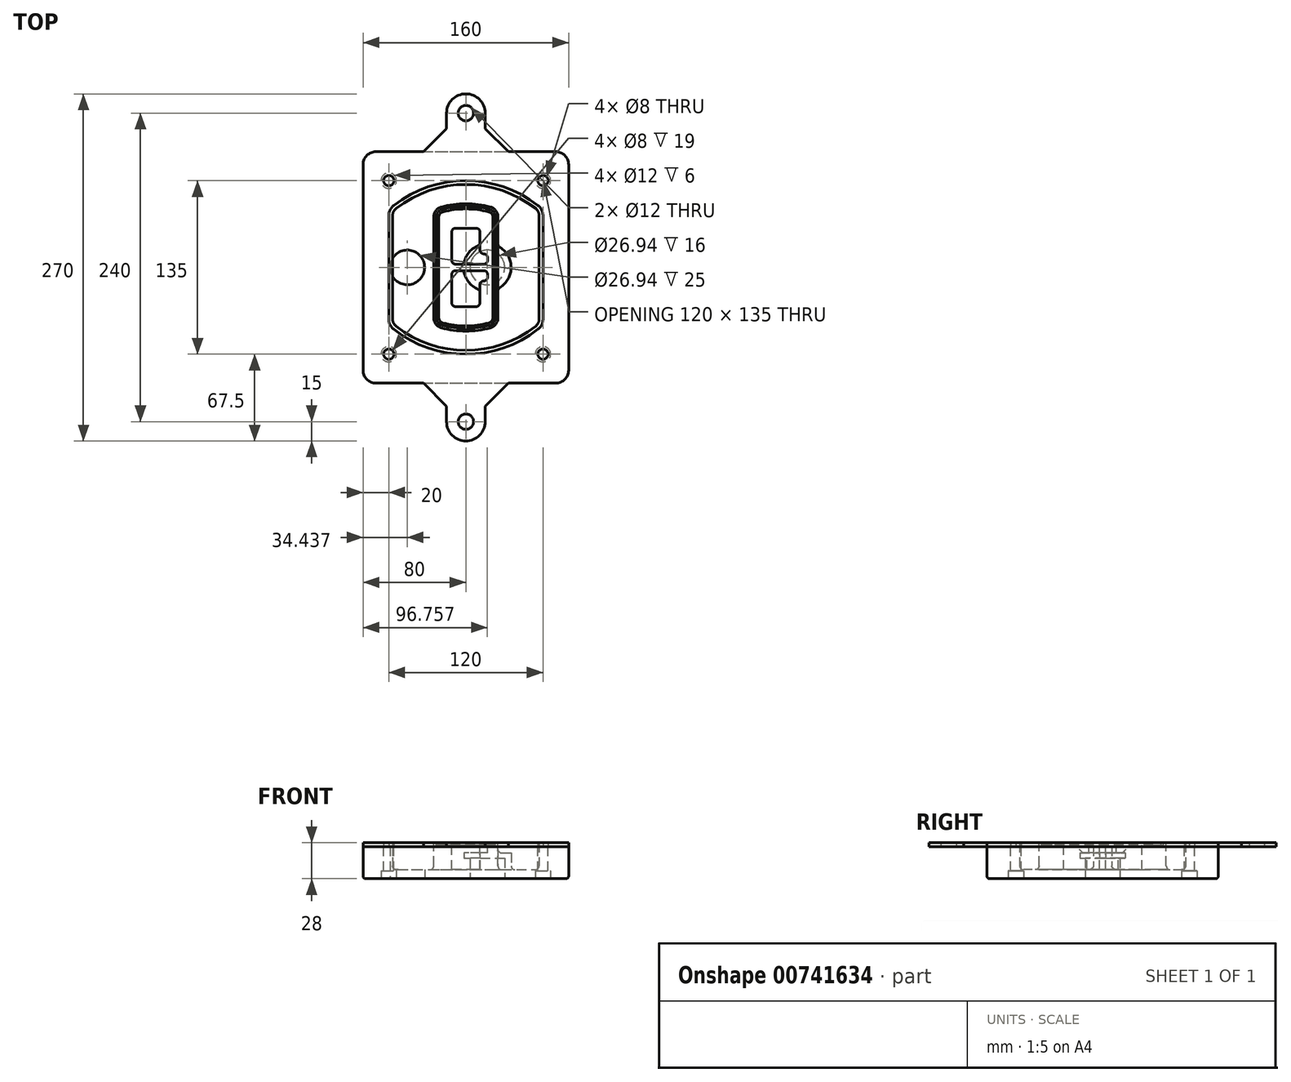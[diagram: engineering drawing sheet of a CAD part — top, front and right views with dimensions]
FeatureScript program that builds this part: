
annotation { "Feature Type Name" : "Feature", "Feature Type Description" : "" }
export const myFeature = defineFeature(function(context is Context, id is Id, definition is map)
    precondition{}
    {
        {
            var Q0;
            Q0=qCreatedBy(makeId("Top.planeOp"),FACE);
            var sketch = newSketch(context, id + "F0", { "sketchPlane" : qUnion([Q0])});
            skPoint(sketch, "E0.rect.middle", {"position": v(0, 0) * mm});
            skLineSegment(sketch, "E1.bottom", {"start": v(-70, -90) * mm, "end": v(70, -90) * mm});
            skLineSegment(sketch, "E1.top", {"start": v(-70, 90) * mm, "end": v(70, 90) * mm});
            skLineSegment(sketch, "E1.left", {"start": v(-80, -80) * mm, "end": v(-80, 80) * mm});
            skLineSegment(sketch, "E1.right", {"start": v(80, -80) * mm, "end": v(80, 80) * mm});
            skLineSegment(sketch, "E2", {"start": v(-80, 90) * mm, "end": v(80, -90) * mm, "construction": true});
            skLineSegment(sketch, "E3", {"start": v(80, 90) * mm, "end": v(-80, -90) * mm, "construction": true});
            skCircle(sketch, "E4", {"center": v(-60, 67.5) * mm, "radius": 4 * mm});
            skCircle(sketch, "E5", {"center": v(60, 67.5) * mm, "radius": 4 * mm});
            skCircle(sketch, "E6", {"center": v(60, -67.5) * mm, "radius": 4 * mm});
            skCircle(sketch, "E7", {"center": v(-60, -67.5) * mm, "radius": 4 * mm});
            skLineSegment(sketch, "E8", {"start": v(-60, 67.5) * mm, "end": v(60, 67.5) * mm, "construction": true});
            skLineSegment(sketch, "E9", {"start": v(60, 67.5) * mm, "end": v(60, -67.5) * mm, "construction": true});
            skLineSegment(sketch, "E10", {"start": v(60, -67.5) * mm, "end": v(-60, -67.5) * mm, "construction": true});
            skLineSegment(sketch, "E11", {"start": v(-60, -67.5) * mm, "end": v(-60, 67.5) * mm, "construction": true});
            skLineSegment(sketch, "E12", {"start": v(-60, 40.3) * mm, "end": v(-60, -40.3) * mm});
            skLineSegment(sketch, "E13", {"start": v(60, 40.3) * mm, "end": v(60, -40.3) * mm});
            skArc(sketch, "E14", {"start": v(56.15, 48.18) * mm, "mid": v(0, 67.5) * mm, "end": v(-56.15, 48.18) * mm});
            skArc(sketch, "E15", {"start": v(-56.15, -48.18) * mm, "mid": v(0, -67.5) * mm, "end": v(56.15, -48.18) * mm});
            skLineSegment(sketch, "E16", {"start": v(-60, 0) * mm, "end": v(60, 0) * mm, "construction": true});
            skPoint(sketch, "E17.visualSharp", {"position": v(-60, -45) * mm});
            skArc(sketch, "E17.filletArc", {"start": v(-60, -40.3) * mm, "mid": v(-58.99, -44.68) * mm, "end": v(-56.15, -48.18) * mm});
            skPoint(sketch, "E18.visualSharp", {"position": v(-60, 45) * mm});
            skArc(sketch, "E18.filletArc", {"start": v(-56.15, 48.18) * mm, "mid": v(-58.99, 44.68) * mm, "end": v(-60, 40.3) * mm});
            skPoint(sketch, "E19.visualSharp", {"position": v(60, 45) * mm});
            skArc(sketch, "E19.filletArc", {"start": v(60, 40.3) * mm, "mid": v(58.99, 44.68) * mm, "end": v(56.15, 48.18) * mm});
            skPoint(sketch, "E20.visualSharp", {"position": v(60, -45) * mm});
            skArc(sketch, "E20.filletArc", {"start": v(56.15, -48.18) * mm, "mid": v(58.99, -44.68) * mm, "end": v(60, -40.3) * mm});
            skPoint(sketch, "E21.visualSharp", {"position": v(-80, 90) * mm});
            skArc(sketch, "E21.filletArc", {"start": v(-70, 90) * mm, "mid": v(-77.07, 87.07) * mm, "end": v(-80, 80) * mm});
            skPoint(sketch, "E22.visualSharp", {"position": v(80, 90) * mm});
            skArc(sketch, "E22.filletArc", {"start": v(80, 80) * mm, "mid": v(77.07, 87.07) * mm, "end": v(70, 90) * mm});
            skPoint(sketch, "E23.visualSharp", {"position": v(80, -90) * mm});
            skArc(sketch, "E23.filletArc", {"start": v(70, -90) * mm, "mid": v(77.07, -87.07) * mm, "end": v(80, -80) * mm});
            skPoint(sketch, "E24.visualSharp", {"position": v(-80, -90) * mm});
            skArc(sketch, "E24.filletArc", {"start": v(-80, -80) * mm, "mid": v(-77.07, -87.07) * mm, "end": v(-70, -90) * mm});
            skArc(sketch, "E25.0", {"start": v(57, 40.3) * mm, "mid": v(56.3, 43.36) * mm, "end": v(54.3, 45.81) * mm});
            skLineSegment(sketch, "E25.1", {"start": v(57, 40.3) * mm, "end": v(57, -40.3) * mm});
            skArc(sketch, "E25.2", {"start": v(54.3, -45.81) * mm, "mid": v(56.3, -43.36) * mm, "end": v(57, -40.3) * mm});
            skArc(sketch, "E25.3", {"start": v(-54.3, -45.81) * mm, "mid": v(0, -64.5) * mm, "end": v(54.3, -45.81) * mm});
            skArc(sketch, "E25.4", {"start": v(-57, -40.3) * mm, "mid": v(-56.3, -43.36) * mm, "end": v(-54.3, -45.81) * mm});
            skArc(sketch, "E25.5", {"start": v(54.3, 45.81) * mm, "mid": v(0, 64.5) * mm, "end": v(-54.3, 45.81) * mm});
            skLineSegment(sketch, "E25.6", {"start": v(-57, 40.3) * mm, "end": v(-57, -40.3) * mm});
            skArc(sketch, "E25.7", {"start": v(-54.3, 45.81) * mm, "mid": v(-56.3, 43.36) * mm, "end": v(-57, 40.3) * mm});
            skArc(sketch, "E26.0", {"start": v(-58.62, 51.33) * mm, "mid": v(-62.58, 46.43) * mm, "end": v(-64, 40.3) * mm});
            skArc(sketch, "E26.1", {"start": v(58.62, 51.33) * mm, "mid": v(0, 71.5) * mm, "end": v(-58.62, 51.33) * mm});
            skArc(sketch, "E26.2", {"start": v(64, 40.3) * mm, "mid": v(62.58, 46.43) * mm, "end": v(58.62, 51.33) * mm});
            skLineSegment(sketch, "E26.3", {"start": v(64, 40.3) * mm, "end": v(64, -40.3) * mm});
            skArc(sketch, "E26.4", {"start": v(58.62, -51.33) * mm, "mid": v(62.58, -46.43) * mm, "end": v(64, -40.3) * mm});
            skLineSegment(sketch, "E26.5", {"start": v(-64, 40.3) * mm, "end": v(-64, -40.3) * mm});
            skArc(sketch, "E26.6", {"start": v(-58.62, -51.33) * mm, "mid": v(0, -71.5) * mm, "end": v(58.62, -51.33) * mm});
            skArc(sketch, "E26.7", {"start": v(-64, -40.3) * mm, "mid": v(-62.58, -46.43) * mm, "end": v(-58.62, -51.33) * mm});
            skSolve(sketch);
        }
        {
            var Q0;
            Q0=makeQuery(id+"F0.imprint","IMPRINT",FACE,{"disambiguationData":[TD([[makeQuery(id+"F0.imprint","IMPRINT",EDGE,{"derivedFrom":sQuery(id+"F0.wireOp",EDGE,"E1.bottom")}),1.0]])]});
            var Q1;
            Q1=makeQuery(id+"F0.imprint","IMPRINT",FACE,{"disambiguationData":[TD([[makeQuery(id+"F0.imprint","IMPRINT",EDGE,{"derivedFrom":sQuery(id+"F0.wireOp",EDGE,"E12")}),1.0]])]});
            var Q2;
            Q2=makeQuery(id+"F0.imprint","IMPRINT",FACE,{"disambiguationData":[TD([[makeQuery(id+"F0.imprint","IMPRINT",EDGE,{"derivedFrom":sQuery(id+"F0.wireOp",EDGE,"E25.0")}),1.0]])]});
            var Q3;
            Q3=makeQuery(id+"F0.imprint","IMPRINT",FACE,{"disambiguationData":[TD([[makeQuery(id+"F0.imprint","IMPRINT",EDGE,{"derivedFrom":sQuery(id+"F0.wireOp",EDGE,"E12")}),-1.0]])]});
            extrude(context, id + "F1", {"entities" : qUnion([Q0, Q1, Q2, Q3]), "oppositeDirection" : true, "depth" : 25 * mm});
        }
        {
            var Q0;
            Q0=makeQuery(id+"F0.imprint","IMPRINT",FACE,{"disambiguationData":[TD([[makeQuery(id+"F0.imprint","IMPRINT",EDGE,{"derivedFrom":sQuery(id+"F0.wireOp",EDGE,"E12")}),1.0]])]});
            extrude(context, id + "F2", {"entities" : qUnion([Q0]), "operationType" : NewBodyOperationType.ADD, "depth" : 3 * mm});
        }
        {
            var Q0;
            Q0=makeQuery(id+"F0.imprint","IMPRINT",FACE,{"disambiguationData":[TD([[makeQuery(id+"F0.imprint","IMPRINT",EDGE,{"derivedFrom":sQuery(id+"F0.wireOp",EDGE,"E25.0")}),1.0]])]});
            extrude(context, id + "F3", {"entities" : qUnion([Q0]), "operationType" : NewBodyOperationType.REMOVE, "oppositeDirection" : true, "depth" : 18 * mm});
        }
        {
            var Q0;
            Q0=makeQuery(id+"F2.opExtrude","CAP_FACE",FACE,{"disambiguationData":[OSD([sQuery(id+"F0.wireOp",EDGE,"E12"),sQuery(id+"F0.wireOp",EDGE,"E13"),sQuery(id+"F0.wireOp",EDGE,"E14"),sQuery(id+"F0.wireOp",EDGE,"E15"),sQuery(id+"F0.wireOp",EDGE,"E17.filletArc"),sQuery(id+"F0.wireOp",EDGE,"E18.filletArc"),sQuery(id+"F0.wireOp",EDGE,"E19.filletArc"),sQuery(id+"F0.wireOp",EDGE,"E20.filletArc"),sQuery(id+"F0.wireOp",EDGE,"E25.0"),sQuery(id+"F0.wireOp",EDGE,"E25.1"),sQuery(id+"F0.wireOp",EDGE,"E25.2"),sQuery(id+"F0.wireOp",EDGE,"E25.3"),sQuery(id+"F0.wireOp",EDGE,"E25.4"),sQuery(id+"F0.wireOp",EDGE,"E25.5"),sQuery(id+"F0.wireOp",EDGE,"E25.6"),sQuery(id+"F0.wireOp",EDGE,"E25.7")])],"isStart":false});
            var sketch = newSketch(context, id + "F4", { "sketchPlane" : qUnion([Q0])});
            skArc(sketch, "E27.0", {"start": v(-19.08, -46.97) * mm, "mid": v(0, -49.5) * mm, "end": v(19.08, -46.97) * mm});
            skArc(sketch, "E28.0", {"start": v(19.08, 46.97) * mm, "mid": v(0, 49.5) * mm, "end": v(-19.08, 46.97) * mm});
            skLineSegment(sketch, "E29", {"start": v(-25, 39.25) * mm, "end": v(-25, -39.25) * mm});
            skLineSegment(sketch, "E30", {"start": v(25, 39.25) * mm, "end": v(25, -39.25) * mm});
            skLineSegment(sketch, "E31", {"start": v(-25, 45.1) * mm, "end": v(25, 45.1) * mm, "construction": true});
            skLineSegment(sketch, "E32", {"start": v(-25, -45.1) * mm, "end": v(25, -45.1) * mm, "construction": true});
            skPoint(sketch, "E33.visualSharp", {"position": v(-25, 45.1) * mm});
            skArc(sketch, "E33.filletArc", {"start": v(-19.08, 46.97) * mm, "mid": v(-23.35, 44.11) * mm, "end": v(-25, 39.25) * mm});
            skPoint(sketch, "E34.visualSharp", {"position": v(25, 45.1) * mm});
            skArc(sketch, "E34.filletArc", {"start": v(25, 39.25) * mm, "mid": v(23.35, 44.11) * mm, "end": v(19.08, 46.97) * mm});
            skPoint(sketch, "E35.visualSharp", {"position": v(25, -45.1) * mm});
            skArc(sketch, "E35.filletArc", {"start": v(19.08, -46.97) * mm, "mid": v(23.35, -44.11) * mm, "end": v(25, -39.25) * mm});
            skPoint(sketch, "E36.visualSharp", {"position": v(-25, -45.1) * mm});
            skArc(sketch, "E36.filletArc", {"start": v(-25, -39.25) * mm, "mid": v(-23.35, -44.11) * mm, "end": v(-19.08, -46.97) * mm});
            skArc(sketch, "E37.0", {"start": v(54.3, 45.81) * mm, "mid": v(0, 64.5) * mm, "end": v(-54.3, 45.81) * mm});
            skArc(sketch, "E37.1", {"start": v(-54.3, 45.81) * mm, "mid": v(-56.3, 43.36) * mm, "end": v(-57, 40.3) * mm});
            skLineSegment(sketch, "E37.2", {"start": v(-57, 40.3) * mm, "end": v(-57, -40.3) * mm});
            skArc(sketch, "E37.3", {"start": v(-57, -40.3) * mm, "mid": v(-56.3, -43.36) * mm, "end": v(-54.3, -45.81) * mm});
            skArc(sketch, "E37.4", {"start": v(-54.3, -45.81) * mm, "mid": v(0, -64.5) * mm, "end": v(54.3, -45.81) * mm});
            skArc(sketch, "E37.5", {"start": v(54.3, -45.81) * mm, "mid": v(56.3, -43.36) * mm, "end": v(57, -40.3) * mm});
            skLineSegment(sketch, "E37.6", {"start": v(57, 40.3) * mm, "end": v(57, -40.3) * mm});
            skArc(sketch, "E37.7", {"start": v(57, 40.3) * mm, "mid": v(56.3, 43.36) * mm, "end": v(54.3, 45.81) * mm});
            skLineSegment(sketch, "E38.0", {"start": v(23, 39.25) * mm, "end": v(23, -39.25) * mm});
            skArc(sketch, "E38.1", {"start": v(18.56, -45.04) * mm, "mid": v(21.76, -42.9) * mm, "end": v(23, -39.25) * mm});
            skArc(sketch, "E38.2", {"start": v(-18.56, -45.04) * mm, "mid": v(0, -47.5) * mm, "end": v(18.56, -45.04) * mm});
            skArc(sketch, "E38.3", {"start": v(-23, -39.25) * mm, "mid": v(-21.76, -42.9) * mm, "end": v(-18.56, -45.04) * mm});
            skLineSegment(sketch, "E38.4", {"start": v(-23, 39.25) * mm, "end": v(-23, -39.25) * mm});
            skArc(sketch, "E38.5", {"start": v(23, 39.25) * mm, "mid": v(21.76, 42.9) * mm, "end": v(18.56, 45.04) * mm});
            skArc(sketch, "E38.6", {"start": v(-18.56, 45.04) * mm, "mid": v(-21.76, 42.9) * mm, "end": v(-23, 39.25) * mm});
            skArc(sketch, "E38.7", {"start": v(18.56, 45.04) * mm, "mid": v(0, 47.5) * mm, "end": v(-18.56, 45.04) * mm});
            skArc(sketch, "E39.0", {"start": v(21, 39.25) * mm, "mid": v(20.18, 41.68) * mm, "end": v(18.04, 43.1) * mm});
            skLineSegment(sketch, "E39.1", {"start": v(21, 39.25) * mm, "end": v(21, -39.25) * mm});
            skArc(sketch, "E39.2", {"start": v(18.04, -43.1) * mm, "mid": v(20.18, -41.68) * mm, "end": v(21, -39.25) * mm});
            skArc(sketch, "E39.3", {"start": v(-18.04, -43.1) * mm, "mid": v(0, -45.5) * mm, "end": v(18.04, -43.1) * mm});
            skArc(sketch, "E39.4", {"start": v(-21, -39.25) * mm, "mid": v(-20.18, -41.68) * mm, "end": v(-18.04, -43.1) * mm});
            skArc(sketch, "E39.5", {"start": v(18.04, 43.1) * mm, "mid": v(0, 45.5) * mm, "end": v(-18.04, 43.1) * mm});
            skLineSegment(sketch, "E39.6", {"start": v(-21, 39.25) * mm, "end": v(-21, -39.25) * mm});
            skArc(sketch, "E39.7", {"start": v(-18.04, 43.1) * mm, "mid": v(-20.18, 41.68) * mm, "end": v(-21, 39.25) * mm});
            skLineSegment(sketch, "E40", {"start": v(-25, 0) * mm, "end": v(25, 0) * mm, "construction": true});
            skLineSegment(sketch, "E41", {"start": v(-11, 5.5) * mm, "end": v(-11, 27.5) * mm});
            skLineSegment(sketch, "E42", {"start": v(-8, 30.5) * mm, "end": v(8, 30.5) * mm});
            skLineSegment(sketch, "E43", {"start": v(11, 27.5) * mm, "end": v(11, 13.5) * mm});
            skLineSegment(sketch, "E44", {"start": v(14, 10.5) * mm, "end": v(14, 10.5) * mm});
            skLineSegment(sketch, "E45", {"start": v(17, 7.5) * mm, "end": v(17, 5.5) * mm});
            skLineSegment(sketch, "E46", {"start": v(14, 2.5) * mm, "end": v(-8, 2.5) * mm});
            skPoint(sketch, "E47.visualSharp", {"position": v(-11, 30.5) * mm});
            skArc(sketch, "E47.filletArc", {"start": v(-8, 30.5) * mm, "mid": v(-10.12, 29.62) * mm, "end": v(-11, 27.5) * mm});
            skPoint(sketch, "E48.visualSharp", {"position": v(11, 30.5) * mm});
            skArc(sketch, "E48.filletArc", {"start": v(11, 27.5) * mm, "mid": v(10.12, 29.62) * mm, "end": v(8, 30.5) * mm});
            skPoint(sketch, "E49.visualSharp", {"position": v(11, 10.5) * mm});
            skArc(sketch, "E49.filletArc", {"start": v(11, 13.5) * mm, "mid": v(11.88, 11.38) * mm, "end": v(14, 10.5) * mm});
            skPoint(sketch, "E50.visualSharp", {"position": v(17, 10.5) * mm});
            skArc(sketch, "E50.filletArc", {"start": v(17, 7.5) * mm, "mid": v(16.12, 9.62) * mm, "end": v(14, 10.5) * mm});
            skPoint(sketch, "E51.visualSharp", {"position": v(17, 2.5) * mm});
            skArc(sketch, "E51.filletArc", {"start": v(14, 2.5) * mm, "mid": v(16.12, 3.38) * mm, "end": v(17, 5.5) * mm});
            skPoint(sketch, "E52.visualSharp", {"position": v(-11, 2.5) * mm});
            skArc(sketch, "E52.filletArc", {"start": v(-11, 5.5) * mm, "mid": v(-10.12, 3.38) * mm, "end": v(-8, 2.5) * mm});
            skLineSegment(sketch, "E53.0.MirrorCS", {"start": v(14, -2.5) * mm, "end": v(-8, -2.5) * mm});
            skArc(sketch, "E54.0.MirrorCS", {"start": v(-11, -5.5) * mm, "mid": v(-10.12, -3.38) * mm, "end": v(-8, -2.5) * mm});
            skLineSegment(sketch, "E55.0.MirrorCS", {"start": v(-11, -5.5) * mm, "end": v(-11, -27.5) * mm});
            skArc(sketch, "E56.0.MirrorCS", {"start": v(-8, -30.5) * mm, "mid": v(-10.12, -29.62) * mm, "end": v(-11, -27.5) * mm});
            skLineSegment(sketch, "E57.0.MirrorCS", {"start": v(-8, -30.5) * mm, "end": v(8, -30.5) * mm});
            skArc(sketch, "E58.0.MirrorCS", {"start": v(11, -27.5) * mm, "mid": v(10.12, -29.62) * mm, "end": v(8, -30.5) * mm});
            skLineSegment(sketch, "E59.0.MirrorCS", {"start": v(11, -27.5) * mm, "end": v(11, -13.5) * mm});
            skArc(sketch, "E60.0.MirrorCS", {"start": v(11, -13.5) * mm, "mid": v(11.88, -11.38) * mm, "end": v(14, -10.5) * mm});
            skArc(sketch, "E61.0.MirrorCS", {"start": v(17, -7.5) * mm, "mid": v(16.12, -9.62) * mm, "end": v(14, -10.5) * mm});
            skLineSegment(sketch, "E62.0.MirrorCS", {"start": v(17, -7.5) * mm, "end": v(17, -5.5) * mm});
            skArc(sketch, "E63.0.MirrorCS", {"start": v(14, -2.5) * mm, "mid": v(16.12, -3.38) * mm, "end": v(17, -5.5) * mm});
            skSolve(sketch);
        }
        {
            var Q0;
            Q0=makeQuery(id+"F4.imprint","IMPRINT",FACE,{"disambiguationData":[TD([[makeQuery(id+"F4.imprint","IMPRINT",EDGE,{"derivedFrom":sQuery(id+"F4.wireOp",EDGE,"E27.0")}),1.0]])]});
            var Q1;
            Q1=makeQuery(id+"F4.imprint","IMPRINT",FACE,{"disambiguationData":[TD([[makeQuery(id+"F4.imprint","IMPRINT",EDGE,{"derivedFrom":sQuery(id+"F4.wireOp",EDGE,"E38.0")}),-1.0]])]});
            var Q2;
            Q2=makeQuery(id+"F4.imprint","IMPRINT",FACE,{"disambiguationData":[TD([[makeQuery(id+"F4.imprint","IMPRINT",EDGE,{"derivedFrom":sQuery(id+"F4.wireOp",EDGE,"E39.0")}),1.0]])]});
            extrude(context, id + "F5", {"entities" : qUnion([Q0, Q1, Q2]), "operationType" : NewBodyOperationType.ADD, "endBound" : BoundingType.UP_TO_NEXT, "oppositeDirection" : true, "depth" : 25 * mm});
        }
        {
            var Q0;
            Q0=makeQuery(id+"F4.imprint","IMPRINT",FACE,{"disambiguationData":[TD([[makeQuery(id+"F4.imprint","IMPRINT",EDGE,{"derivedFrom":sQuery(id+"F4.wireOp",EDGE,"E38.0")}),-1.0]])]});
            extrude(context, id + "F6", {"entities" : qUnion([Q0]), "operationType" : NewBodyOperationType.REMOVE, "oppositeDirection" : true, "depth" : 2 * mm});
        }
        {
            var Q0;
            Q0=makeQuery(id+"F1.opExtrude","CAP_FACE",FACE,{"disambiguationData":[OSD([sQuery(id+"F0.wireOp",EDGE,"E1.bottom"),sQuery(id+"F0.wireOp",EDGE,"E1.top"),sQuery(id+"F0.wireOp",EDGE,"E1.left"),sQuery(id+"F0.wireOp",EDGE,"E1.right"),sQuery(id+"F0.wireOp",EDGE,"E4"),sQuery(id+"F0.wireOp",EDGE,"E5"),sQuery(id+"F0.wireOp",EDGE,"E6"),sQuery(id+"F0.wireOp",EDGE,"E7"),sQuery(id+"F0.wireOp",EDGE,"E21.filletArc"),sQuery(id+"F0.wireOp",EDGE,"E22.filletArc"),sQuery(id+"F0.wireOp",EDGE,"E23.filletArc"),sQuery(id+"F0.wireOp",EDGE,"E24.filletArc")])],"isStart":false});
            var sketch = newSketch(context, id + "F7", { "sketchPlane" : qUnion([Q0])});
            skCircle(sketch, "E64", {"center": v(16.76, 0) * mm, "radius": 13.47 * mm});
            skCircle(sketch, "E65", {"center": v(-45.56, 0) * mm, "radius": 13.47 * mm});
            skLineSegment(sketch, "E66", {"start": v(80, 0) * mm, "end": v(-80, 0) * mm});
            skCircle(sketch, "E67", {"center": v(16.76, 0) * mm, "radius": 18.47 * mm});
            skCircle(sketch, "E68", {"center": v(60, -67.5) * mm, "radius": 6 * mm});
            skCircle(sketch, "E69", {"center": v(-60, -67.5) * mm, "radius": 6 * mm});
            skCircle(sketch, "E70", {"center": v(-60, 67.5) * mm, "radius": 6 * mm});
            skCircle(sketch, "E71", {"center": v(60, 67.5) * mm, "radius": 6 * mm});
            skSolve(sketch);
        }
        {
            var Q0;
            {var subQ1=sQuery(id+"F7.wireOp",EDGE,"E66");var subQ4=sQuery(id+"F7.wireOp",EDGE,"E64");var subQ6=makeQuery(id+"F7.imprint","INTERSECT",VERTEX,{"disambiguationData":[OD(0.0)],"derivedFrom":[subQ4,subQ1]});Q0=makeQuery(id+"F7.imprint","IMPRINT",FACE,{"disambiguationData":[TD([[makeQuery(id+"F7.imprint","IMPRINT",EDGE,{"disambiguationData":[TD([[subQ6,-1.0]])],"derivedFrom":subQ4}),-1.0]])]});}
            var Q1;
            {var subQ0=sQuery(id+"F7.wireOp",EDGE,"E66");var subQ1=sQuery(id+"F7.wireOp",EDGE,"E64");var subQ3=makeQuery(id+"F7.imprint","INTERSECT",VERTEX,{"disambiguationData":[OD(0.0)],"derivedFrom":[subQ1,subQ0]});Q1=makeQuery(id+"F7.imprint","IMPRINT",FACE,{"disambiguationData":[TD([[makeQuery(id+"F7.imprint","IMPRINT",EDGE,{"disambiguationData":[TD([[subQ3,-1.0]])],"derivedFrom":subQ1}),1.0]])]});}
            var Q2;
            {var subQ0=sQuery(id+"F7.wireOp",EDGE,"E66");var subQ1=sQuery(id+"F7.wireOp",EDGE,"E64");var subQ3=makeQuery(id+"F7.imprint","INTERSECT",VERTEX,{"disambiguationData":[OD(0.0)],"derivedFrom":[subQ1,subQ0]});Q2=makeQuery(id+"F7.imprint","IMPRINT",FACE,{"disambiguationData":[TD([[makeQuery(id+"F7.imprint","IMPRINT",EDGE,{"disambiguationData":[TD([[subQ3,1.0]])],"derivedFrom":subQ1}),1.0]])]});}
            var Q3;
            {var subQ1=sQuery(id+"F7.wireOp",EDGE,"E66");var subQ4=sQuery(id+"F7.wireOp",EDGE,"E64");var subQ6=makeQuery(id+"F7.imprint","INTERSECT",VERTEX,{"disambiguationData":[OD(0.0)],"derivedFrom":[subQ4,subQ1]});Q3=makeQuery(id+"F7.imprint","IMPRINT",FACE,{"disambiguationData":[TD([[makeQuery(id+"F7.imprint","IMPRINT",EDGE,{"disambiguationData":[TD([[subQ6,1.0]])],"derivedFrom":subQ4}),-1.0]])]});}
            extrude(context, id + "F8", {"entities" : qUnion([Q0, Q1, Q2, Q3]), "operationType" : NewBodyOperationType.ADD, "oppositeDirection" : true, "depth" : 20 * mm});
        }
        {
            var Q0;
            {var subQ0=sQuery(id+"F7.wireOp",EDGE,"E66");var subQ1=sQuery(id+"F7.wireOp",EDGE,"E64");var subQ3=makeQuery(id+"F7.imprint","INTERSECT",VERTEX,{"disambiguationData":[OD(0.0)],"derivedFrom":[subQ1,subQ0]});Q0=makeQuery(id+"F7.imprint","IMPRINT",FACE,{"disambiguationData":[TD([[makeQuery(id+"F7.imprint","IMPRINT",EDGE,{"disambiguationData":[TD([[subQ3,-1.0]])],"derivedFrom":subQ1}),1.0]])]});}
            var Q1;
            {var subQ0=sQuery(id+"F7.wireOp",EDGE,"E66");var subQ1=sQuery(id+"F7.wireOp",EDGE,"E64");var subQ3=makeQuery(id+"F7.imprint","INTERSECT",VERTEX,{"disambiguationData":[OD(0.0)],"derivedFrom":[subQ1,subQ0]});Q1=makeQuery(id+"F7.imprint","IMPRINT",FACE,{"disambiguationData":[TD([[makeQuery(id+"F7.imprint","IMPRINT",EDGE,{"disambiguationData":[TD([[subQ3,1.0]])],"derivedFrom":subQ1}),1.0]])]});}
            extrude(context, id + "F9", {"entities" : qUnion([Q0, Q1]), "operationType" : NewBodyOperationType.REMOVE, "oppositeDirection" : true, "depth" : 16 * mm});
        }
        {
            var Q0;
            {var subQ0=sQuery(id+"F7.wireOp",EDGE,"E66");var subQ1=sQuery(id+"F7.wireOp",EDGE,"E65");var subQ3=makeQuery(id+"F7.imprint","INTERSECT",VERTEX,{"disambiguationData":[OD(0.0)],"derivedFrom":[subQ1,subQ0]});Q0=makeQuery(id+"F7.imprint","IMPRINT",FACE,{"disambiguationData":[TD([[makeQuery(id+"F7.imprint","IMPRINT",EDGE,{"disambiguationData":[TD([[subQ3,-1.0]])],"derivedFrom":subQ1}),1.0]])]});}
            var Q1;
            {var subQ0=sQuery(id+"F7.wireOp",EDGE,"E66");var subQ1=sQuery(id+"F7.wireOp",EDGE,"E65");var subQ3=makeQuery(id+"F7.imprint","INTERSECT",VERTEX,{"disambiguationData":[OD(0.0)],"derivedFrom":[subQ1,subQ0]});Q1=makeQuery(id+"F7.imprint","IMPRINT",FACE,{"disambiguationData":[TD([[makeQuery(id+"F7.imprint","IMPRINT",EDGE,{"disambiguationData":[TD([[subQ3,1.0]])],"derivedFrom":subQ1}),1.0]])]});}
            extrude(context, id + "F10", {"entities" : qUnion([Q0, Q1]), "operationType" : NewBodyOperationType.REMOVE, "oppositeDirection" : true, "depth" : 25 * mm});
        }
        {
            var Q0;
            Q0=makeQuery(id+"F7.imprint","IMPRINT",FACE,{"disambiguationData":[TD([[makeQuery(id+"F7.imprint","IMPRINT",EDGE,{"derivedFrom":sQuery(id+"F7.wireOp",EDGE,"E68")}),1.0]])]});
            var Q1;
            Q1=makeQuery(id+"F7.imprint","IMPRINT",FACE,{"disambiguationData":[TD([[makeQuery(id+"F7.imprint","IMPRINT",EDGE,{"derivedFrom":makeQuery(id+"F1.opExtrude","CAP_EDGE",EDGE,{"disambiguationData":[OSD([sQuery(id+"F0.wireOp",EDGE,"E5")])],"isStart":false})}),-1.0]])]});
            var Q2;
            Q2=makeQuery(id+"F7.imprint","IMPRINT",FACE,{"disambiguationData":[TD([[makeQuery(id+"F7.imprint","IMPRINT",EDGE,{"derivedFrom":sQuery(id+"F7.wireOp",EDGE,"E69")}),1.0]])]});
            var Q3;
            Q3=makeQuery(id+"F7.imprint","IMPRINT",FACE,{"disambiguationData":[TD([[makeQuery(id+"F7.imprint","IMPRINT",EDGE,{"derivedFrom":makeQuery(id+"F1.opExtrude","CAP_EDGE",EDGE,{"disambiguationData":[OSD([sQuery(id+"F0.wireOp",EDGE,"E4")])],"isStart":false})}),-1.0]])]});
            var Q4;
            Q4=makeQuery(id+"F7.imprint","IMPRINT",FACE,{"disambiguationData":[TD([[makeQuery(id+"F7.imprint","IMPRINT",EDGE,{"derivedFrom":sQuery(id+"F7.wireOp",EDGE,"E70")}),1.0]])]});
            var Q5;
            Q5=makeQuery(id+"F7.imprint","IMPRINT",FACE,{"disambiguationData":[TD([[makeQuery(id+"F7.imprint","IMPRINT",EDGE,{"derivedFrom":makeQuery(id+"F1.opExtrude","CAP_EDGE",EDGE,{"disambiguationData":[OSD([sQuery(id+"F0.wireOp",EDGE,"E7")])],"isStart":false})}),-1.0]])]});
            var Q6;
            Q6=makeQuery(id+"F7.imprint","IMPRINT",FACE,{"disambiguationData":[TD([[makeQuery(id+"F7.imprint","IMPRINT",EDGE,{"derivedFrom":sQuery(id+"F7.wireOp",EDGE,"E71")}),1.0]])]});
            var Q7;
            Q7=makeQuery(id+"F7.imprint","IMPRINT",FACE,{"disambiguationData":[TD([[makeQuery(id+"F7.imprint","IMPRINT",EDGE,{"derivedFrom":makeQuery(id+"F1.opExtrude","CAP_EDGE",EDGE,{"disambiguationData":[OSD([sQuery(id+"F0.wireOp",EDGE,"E6")])],"isStart":false})}),-1.0]])]});
            extrude(context, id + "F11", {"entities" : qUnion([Q0, Q1, Q2, Q3, Q4, Q5, Q6, Q7]), "operationType" : NewBodyOperationType.REMOVE, "oppositeDirection" : true, "depth" : 6 * mm});
        }
        {
            var Q0;
            Q0=makeQuery(id+"F9.boolean.opBoolean","COPY",FACE,{"derivedFrom":makeQuery(id+"F9.opExtrude","CAP_FACE",FACE,{"disambiguationData":[OSD([sQuery(id+"F7.wireOp",EDGE,"E64")])],"isStart":false})});
            var sketch = newSketch(context, id + "F12", { "sketchPlane" : qUnion([Q0])});
            skArc(sketch, "E72.0", {"start": v(11, 17.55) * mm, "mid": v(2.57, 11.82) * mm, "end": v(-1.54, 2.5) * mm});
            skArc(sketch, "E72.1", {"start": v(-1.54, -2.5) * mm, "mid": v(2.57, -11.82) * mm, "end": v(11, -17.55) * mm});
            skLineSegment(sketch, "E73", {"start": v(-1.54, -2.5) * mm, "end": v(14, -2.5) * mm});
            skLineSegment(sketch, "E74.0", {"start": v(14, 2.5) * mm, "end": v(-1.54, 2.5) * mm});
            skArc(sketch, "E74.1", {"start": v(14, 2.5) * mm, "mid": v(16.12, 3.38) * mm, "end": v(17, 5.5) * mm});
            skLineSegment(sketch, "E74.2", {"start": v(17, 7.5) * mm, "end": v(17, 5.5) * mm});
            skArc(sketch, "E74.3", {"start": v(17, 7.5) * mm, "mid": v(16.12, 9.62) * mm, "end": v(14, 10.5) * mm});
            skArc(sketch, "E74.4", {"start": v(11, 13.5) * mm, "mid": v(11.88, 11.38) * mm, "end": v(14, 10.5) * mm});
            skLineSegment(sketch, "E74.5", {"start": v(11, 17.55) * mm, "end": v(11, 13.5) * mm});
            skLineSegment(sketch, "E74.7", {"start": v(14, -2.5) * mm, "end": v(-1.54, -2.5) * mm});
            skArc(sketch, "E74.8", {"start": v(14, -2.5) * mm, "mid": v(16.12, -3.38) * mm, "end": v(17, -5.5) * mm});
            skLineSegment(sketch, "E74.9", {"start": v(17, -7.5) * mm, "end": v(17, -5.5) * mm});
            skArc(sketch, "E74.10", {"start": v(17, -7.5) * mm, "mid": v(16.12, -9.62) * mm, "end": v(14, -10.5) * mm});
            skArc(sketch, "E74.11", {"start": v(11, -13.5) * mm, "mid": v(11.88, -11.38) * mm, "end": v(14, -10.5) * mm});
            skLineSegment(sketch, "E74.12", {"start": v(11, -17.55) * mm, "end": v(11, -13.5) * mm});
            skPoint(sketch, "E75.orphan", {"position": v(11, -27.5) * mm});
            skPoint(sketch, "E76.orphan", {"position": v(-8, -2.5) * mm});
            skPoint(sketch, "E77.orphan", {"position": v(-8, 2.5) * mm});
            skPoint(sketch, "E78.orphan", {"position": v(11, 27.5) * mm});
            skSolve(sketch);
        }
        {
            var Q0;
            {var subQ7=sQuery(id+"F12.wireOp",EDGE,"E72.0");var subQ14=sQuery(id+"F12.wireOp",EDGE,"E72.1");var subQ16=sQuery(id+"F12.wireOp",EDGE,"E74.1");var subQ18=sQuery(id+"F12.wireOp",EDGE,"E74.8");Q0=qUnion([makeQuery(id+"F12.imprint","IMPRINT",FACE,{"disambiguationData":[TD([[makeQuery(id+"F12.imprint","IMPRINT",EDGE,{"derivedFrom":subQ7}),1.0]])]}),makeQuery(id+"F12.imprint","IMPRINT",FACE,{"disambiguationData":[TD([[makeQuery(id+"F12.imprint","IMPRINT",EDGE,{"derivedFrom":subQ14}),1.0]])]}),makeQuery(id+"F12.imprint","IMPRINT",FACE,{"disambiguationData":[TD([[makeQuery(id+"F12.imprint","IMPRINT",EDGE,{"derivedFrom":subQ16}),1.0]])]}),makeQuery(id+"F12.imprint","IMPRINT",FACE,{"disambiguationData":[TD([[makeQuery(id+"F12.imprint","IMPRINT",EDGE,{"derivedFrom":subQ18}),-1.0]])]})]);}
            var Q1;
            Q1=makeQuery(id+"F5.boolean.opBoolean","SPLIT",FACE,{"disambiguationData":[TD([makeQuery(id+"F5.opExtrude","SWEPT_FACE",FACE,{"disambiguationData":[OSD([sQuery(id+"F4.wireOp",EDGE,"E41")])]})])],"derivedFrom":makeQuery(id+"F3.boolean.opBoolean","COPY",FACE,{"derivedFrom":makeQuery(id+"F3.opExtrude","CAP_FACE",FACE,{"disambiguationData":[OSD([sQuery(id+"F0.wireOp",EDGE,"E25.0"),sQuery(id+"F0.wireOp",EDGE,"E25.1"),sQuery(id+"F0.wireOp",EDGE,"E25.2"),sQuery(id+"F0.wireOp",EDGE,"E25.3"),sQuery(id+"F0.wireOp",EDGE,"E25.4"),sQuery(id+"F0.wireOp",EDGE,"E25.5"),sQuery(id+"F0.wireOp",EDGE,"E25.6"),sQuery(id+"F0.wireOp",EDGE,"E25.7")])],"isStart":false})})});
            extrude(context, id + "F13", {"entities" : qUnion([Q0]), "operationType" : NewBodyOperationType.REMOVE, "endBound" : BoundingType.UP_TO_SURFACE, "endBoundEntityFace" : qUnion([Q1]), "depth" : 25 * mm});
        }
        {
            var Q0;
            Q0=makeQuery(id+"F3.boolean.opBoolean","COPY",EDGE,{"derivedFrom":makeQuery(id+"F3.opExtrude","CAP_EDGE",EDGE,{"disambiguationData":[OSD([sQuery(id+"F0.wireOp",EDGE,"E25.6")])],"isStart":false})});
            var Q1;
            Q1=makeQuery(id+"F8.boolean.opBoolean","INTERSECT",EDGE,{"derivedFrom":[makeQuery(id+"F5.opExtrude","SWEPT_FACE",FACE,{"disambiguationData":[OSD([sQuery(id+"F4.wireOp",EDGE,"E30")])]}),makeQuery(id+"F8.opExtrude","CAP_FACE",FACE,{"disambiguationData":[OSD([sQuery(id+"F7.wireOp",EDGE,"E67")])],"isStart":false})]});
            var Q2;
            Q2=makeQuery(id+"F8.boolean.opBoolean","INTERSECT",EDGE,{"disambiguationData":[OD(1.0)],"derivedFrom":[makeQuery(id+"F5.opExtrude","SWEPT_FACE",FACE,{"disambiguationData":[OSD([sQuery(id+"F4.wireOp",EDGE,"E30")])]}),makeQuery(id+"F8.opExtrude","SWEPT_FACE",FACE,{"disambiguationData":[OSD([sQuery(id+"F7.wireOp",EDGE,"E67")])]})]});
            var Q3;
            {var subQ0=sQuery(id+"F4.wireOp",EDGE,"E30");Q3=makeQuery(id+"F8.boolean.opBoolean","SPLIT",EDGE,{"disambiguationData":[TD([makeQuery(id+"F5.opExtrude","SWEPT_FACE",FACE,{"disambiguationData":[OSD([sQuery(id+"F4.wireOp",EDGE,"E35.filletArc")])]})])],"derivedFrom":makeQuery(id+"F5.opExtrude","CAP_EDGE",EDGE,{"disambiguationData":[OSD([subQ0])],"isStart":false})});}
            var Q4;
            {var subQ0=sQuery(id+"F0.wireOp",EDGE,"E25.7");var subQ1=sQuery(id+"F0.wireOp",EDGE,"E25.1");var subQ2=sQuery(id+"F0.wireOp",EDGE,"E25.6");var subQ3=sQuery(id+"F0.wireOp",EDGE,"E25.5");var subQ4=sQuery(id+"F0.wireOp",EDGE,"E25.4");var subQ5=sQuery(id+"F0.wireOp",EDGE,"E25.0");var subQ6=sQuery(id+"F0.wireOp",EDGE,"E25.2");var subQ7=sQuery(id+"F0.wireOp",EDGE,"E25.3");Q4=makeQuery(id+"F8.boolean.opBoolean","INTERSECT",EDGE,{"derivedFrom":[makeQuery(id+"F5.boolean.opBoolean","SPLIT",FACE,{"disambiguationData":[TD([makeQuery(id+"F2.opExtrude","SWEPT_FACE",FACE,{"disambiguationData":[OSD([subQ5])]})])],"derivedFrom":makeQuery(id+"F3.boolean.opBoolean","COPY",FACE,{"derivedFrom":makeQuery(id+"F3.opExtrude","CAP_FACE",FACE,{"disambiguationData":[OSD([subQ5,subQ1,subQ6,subQ7,subQ4,subQ3,subQ2,subQ0])],"isStart":false})})}),makeQuery(id+"F8.opExtrude","SWEPT_FACE",FACE,{"disambiguationData":[OSD([sQuery(id+"F7.wireOp",EDGE,"E67")])]})]});}
            var Q5;
            Q5=makeQuery(id+"F8.boolean.opBoolean","INTERSECT",EDGE,{"disambiguationData":[OD(0.0)],"derivedFrom":[makeQuery(id+"F5.opExtrude","SWEPT_FACE",FACE,{"disambiguationData":[OSD([sQuery(id+"F4.wireOp",EDGE,"E30")])]}),makeQuery(id+"F8.opExtrude","SWEPT_FACE",FACE,{"disambiguationData":[OSD([sQuery(id+"F7.wireOp",EDGE,"E67")])]})]});
            fillet(context, id + "F14", {"entities" : qUnion([Q0, Q1, Q2, Q3, Q4, Q5]), "radius" : 3 * mm, "tangentPropagation" : true, "allowEdgeOverflow" : false});
        }
        {
            var Q0;
            Q0=makeQuery(id+"F1.opExtrude","CAP_EDGE",EDGE,{"disambiguationData":[OSD([sQuery(id+"F0.wireOp",EDGE,"E1.bottom")])],"isStart":false});
            fillet(context, id + "F15", {"entities" : qUnion([Q0]), "radius" : 2 * mm, "tangentPropagation" : true, "allowEdgeOverflow" : false});
        }
        {
            var Q0;
            {var subQ0=sQuery(id+"F0.wireOp",EDGE,"E21.filletArc");var subQ1=sQuery(id+"F0.wireOp",EDGE,"E7");var subQ2=sQuery(id+"F0.wireOp",EDGE,"E6");var subQ3=sQuery(id+"F0.wireOp",EDGE,"E5");var subQ4=sQuery(id+"F0.wireOp",EDGE,"E4");var subQ5=sQuery(id+"F0.wireOp",EDGE,"E22.filletArc");var subQ6=sQuery(id+"F0.wireOp",EDGE,"E1.bottom");var subQ7=sQuery(id+"F0.wireOp",EDGE,"E1.right");var subQ8=sQuery(id+"F0.wireOp",EDGE,"E1.top");var subQ9=sQuery(id+"F0.wireOp",EDGE,"E1.left");var subQ10=sQuery(id+"F0.wireOp",EDGE,"E23.filletArc");var subQ11=sQuery(id+"F0.wireOp",EDGE,"E24.filletArc");Q0=makeQuery(id+"F2.boolean.opBoolean","SPLIT",FACE,{"disambiguationData":[TD([makeQuery(id+"F1.opExtrude","SWEPT_FACE",FACE,{"disambiguationData":[OSD([subQ6])]})])],"derivedFrom":makeQuery(id+"F1.opExtrude","CAP_FACE",FACE,{"disambiguationData":[OSD([subQ6,subQ8,subQ9,subQ7,subQ4,subQ3,subQ2,subQ1,subQ0,subQ5,subQ10,subQ11])],"isStart":true})});}
            var sketch = newSketch(context, id + "F16", { "sketchPlane" : qUnion([Q0])});
            skLineSegment(sketch, "E79.0", {"start": v(-70, 90) * mm, "end": v(70, 90) * mm});
            skCircle(sketch, "E79.1", {"center": v(-60, 67.5) * mm, "radius": 4 * mm});
            skArc(sketch, "E79.2", {"start": v(-70, 90) * mm, "mid": v(-77.07, 87.07) * mm, "end": v(-80, 80) * mm});
            skLineSegment(sketch, "E79.3", {"start": v(-80, -80) * mm, "end": v(-80, 80) * mm});
            skArc(sketch, "E79.4", {"start": v(-80, -80) * mm, "mid": v(-77.07, -87.07) * mm, "end": v(-70, -90) * mm});
            skLineSegment(sketch, "E79.5", {"start": v(-70, -90) * mm, "end": v(70, -90) * mm});
            skArc(sketch, "E79.6", {"start": v(70, -90) * mm, "mid": v(77.07, -87.07) * mm, "end": v(80, -80) * mm});
            skLineSegment(sketch, "E79.7", {"start": v(80, -80) * mm, "end": v(80, 80) * mm});
            skArc(sketch, "E79.8", {"start": v(80, 80) * mm, "mid": v(77.07, 87.07) * mm, "end": v(70, 90) * mm});
            skCircle(sketch, "E79.9", {"center": v(60, 67.5) * mm, "radius": 4 * mm});
            skCircle(sketch, "E79.10", {"center": v(60, -67.5) * mm, "radius": 4 * mm});
            skCircle(sketch, "E79.11", {"center": v(-60, -67.5) * mm, "radius": 4 * mm});
            skLineSegment(sketch, "E79.12", {"start": v(-60, 40.3) * mm, "end": v(-60, -40.3) * mm});
            skArc(sketch, "E79.13", {"start": v(56.15, 48.18) * mm, "mid": v(0, 67.5) * mm, "end": v(-56.15, 48.18) * mm});
            skLineSegment(sketch, "E79.14", {"start": v(60, 40.3) * mm, "end": v(60, -40.3) * mm});
            skArc(sketch, "E79.15", {"start": v(-56.15, -48.18) * mm, "mid": v(0, -67.5) * mm, "end": v(56.15, -48.18) * mm});
            skArc(sketch, "E79.16", {"start": v(56.15, -48.18) * mm, "mid": v(58.99, -44.68) * mm, "end": v(60, -40.3) * mm});
            skArc(sketch, "E79.17", {"start": v(-60, -40.3) * mm, "mid": v(-58.99, -44.68) * mm, "end": v(-56.15, -48.18) * mm});
            skArc(sketch, "E79.18", {"start": v(-56.15, 48.18) * mm, "mid": v(-58.99, 44.68) * mm, "end": v(-60, 40.3) * mm});
            skArc(sketch, "E79.19", {"start": v(60, 40.3) * mm, "mid": v(58.99, 44.68) * mm, "end": v(56.15, 48.18) * mm});
            skLineSegment(sketch, "E80", {"start": v(0, 90) * mm, "end": v(0, 120) * mm, "construction": true});
            skCircle(sketch, "E81", {"center": v(0, 120) * mm, "radius": 6 * mm});
            skLineSegment(sketch, "E82", {"start": v(-15, 108) * mm, "end": v(-15, 120) * mm});
            skLineSegment(sketch, "E83", {"start": v(15, 108) * mm, "end": v(15, 120) * mm});
            skArc(sketch, "E84", {"start": v(15, 120) * mm, "mid": v(0, 135) * mm, "end": v(-15, 120) * mm});
            skLineSegment(sketch, "E85", {"start": v(-15, 108) * mm, "end": v(-33, 90) * mm});
            skLineSegment(sketch, "E86", {"start": v(15, 108) * mm, "end": v(33, 90) * mm});
            skLineSegment(sketch, "E87", {"start": v(-80, 0) * mm, "end": v(80, 0) * mm, "construction": true});
            skLineSegment(sketch, "E88.MirrorCS", {"start": v(15, -108) * mm, "end": v(33, -90) * mm});
            skLineSegment(sketch, "E89.MirrorCS", {"start": v(15, -108) * mm, "end": v(15, -120) * mm});
            skArc(sketch, "E90.MirrorCS", {"start": v(15, -120) * mm, "mid": v(0, -135) * mm, "end": v(-15, -120) * mm});
            skLineSegment(sketch, "E91.MirrorCS", {"start": v(-15, -108) * mm, "end": v(-15, -120) * mm});
            skLineSegment(sketch, "E92.MirrorCS", {"start": v(-15, -108) * mm, "end": v(-33, -90) * mm});
            skLineSegment(sketch, "E93.MirrorCS", {"start": v(0, -90) * mm, "end": v(0, -120) * mm, "construction": true});
            skCircle(sketch, "E94.MirrorC", {"center": v(0, -120) * mm, "radius": 6 * mm});
            skSolve(sketch);
        }
        {
            var Q0;
            Q0 = qSketchRegion(id + "F16", true);
            var Q1;
            Q1=makeQuery(id+"F2.opExtrude","CAP_FACE",FACE,{"disambiguationData":[OSD([sQuery(id+"F0.wireOp",EDGE,"E12"),sQuery(id+"F0.wireOp",EDGE,"E13"),sQuery(id+"F0.wireOp",EDGE,"E14"),sQuery(id+"F0.wireOp",EDGE,"E15"),sQuery(id+"F0.wireOp",EDGE,"E17.filletArc"),sQuery(id+"F0.wireOp",EDGE,"E18.filletArc"),sQuery(id+"F0.wireOp",EDGE,"E19.filletArc"),sQuery(id+"F0.wireOp",EDGE,"E20.filletArc"),sQuery(id+"F0.wireOp",EDGE,"E25.0"),sQuery(id+"F0.wireOp",EDGE,"E25.1"),sQuery(id+"F0.wireOp",EDGE,"E25.2"),sQuery(id+"F0.wireOp",EDGE,"E25.3"),sQuery(id+"F0.wireOp",EDGE,"E25.4"),sQuery(id+"F0.wireOp",EDGE,"E25.5"),sQuery(id+"F0.wireOp",EDGE,"E25.6"),sQuery(id+"F0.wireOp",EDGE,"E25.7")])],"isStart":false});
            extrude(context, id + "F17", {"entities" : qUnion([Q0]), "endBound" : BoundingType.UP_TO_SURFACE, "depth" : 25 * mm, "endBoundEntityFace" : qUnion([Q1]), "offsetDistance" : 25 * mm});
        }
    });
